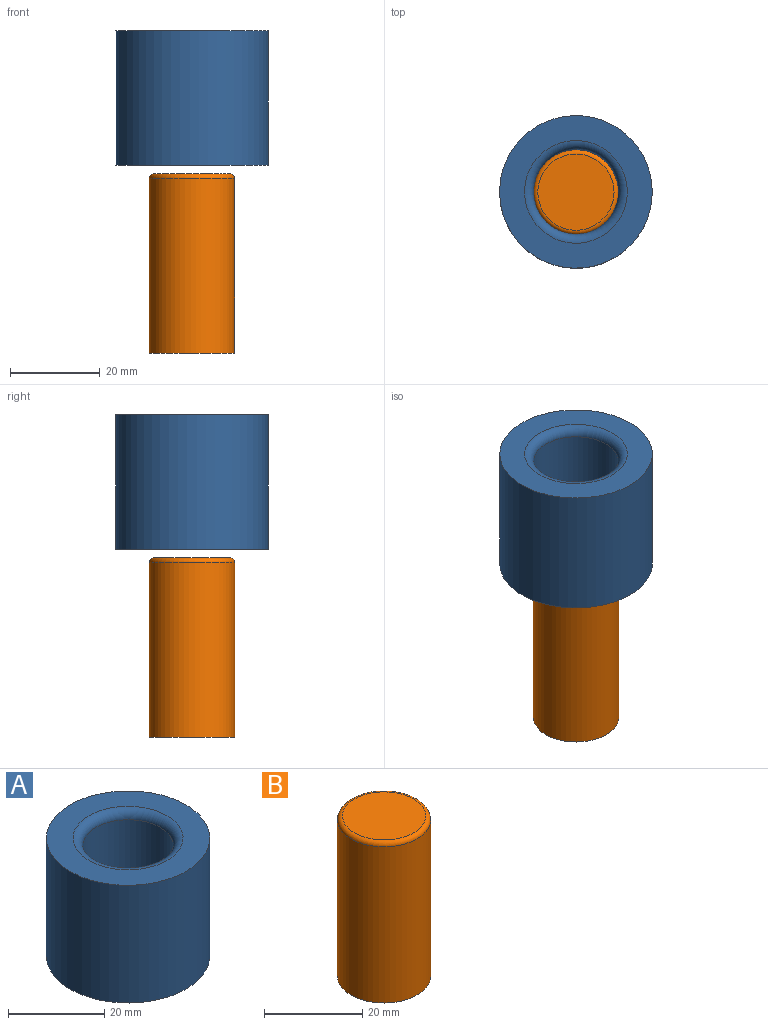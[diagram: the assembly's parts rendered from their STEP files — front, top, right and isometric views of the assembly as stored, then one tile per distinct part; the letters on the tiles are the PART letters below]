
ASSEMBLY  parts=2 mates=1
PART A: 6 faces, bbox 34x34x30 mm
  f0: cylinder r=9.45mm len=26mm, axis (0,0,-1), area 1543.8mm2, adj f4,f5
  f1: cylinder r=17mm len=34mm, axis (0,0,-1), area 3204.4mm2, adj f2,f3
  f2: plane 34x34mm, normal (0,0,1), area 496mm2, adj f1,f5
  f3: plane 34x34mm, normal (0,0,-1), area 496mm2, adj f1,f4
  f4: torus R=11.45mm, axis (0,0,1), area 200.9mm2, adj f0,f3
  f5: torus R=11.45mm, axis (0,0,1), area 200.9mm2, adj f0,f2
PART B: 4 faces, bbox 20.6x20.6x40 mm
  f0: cylinder r=9.5mm len=39mm, axis (0,0,-1), area 2327.3mm2, adj f2,f3
  f1: plane 17x17mm, normal (0,0,1), area 226.8mm2, adj f3
  f2: plane 19x19mm, normal (0,0,-1), area 283.4mm2, adj f0
  f3: torus R=8.5mm, axis (0,0,1), area 90.2mm2, adj f0,f1
PLACE A t=(-22.59,10.61,35)mm
PLACE B t=(-22.59,10.61,-6.91)mm
MATE slider A.f0 <-> B.f0  axis (0,0,-1) through (-22.59,10.61,50)mm
